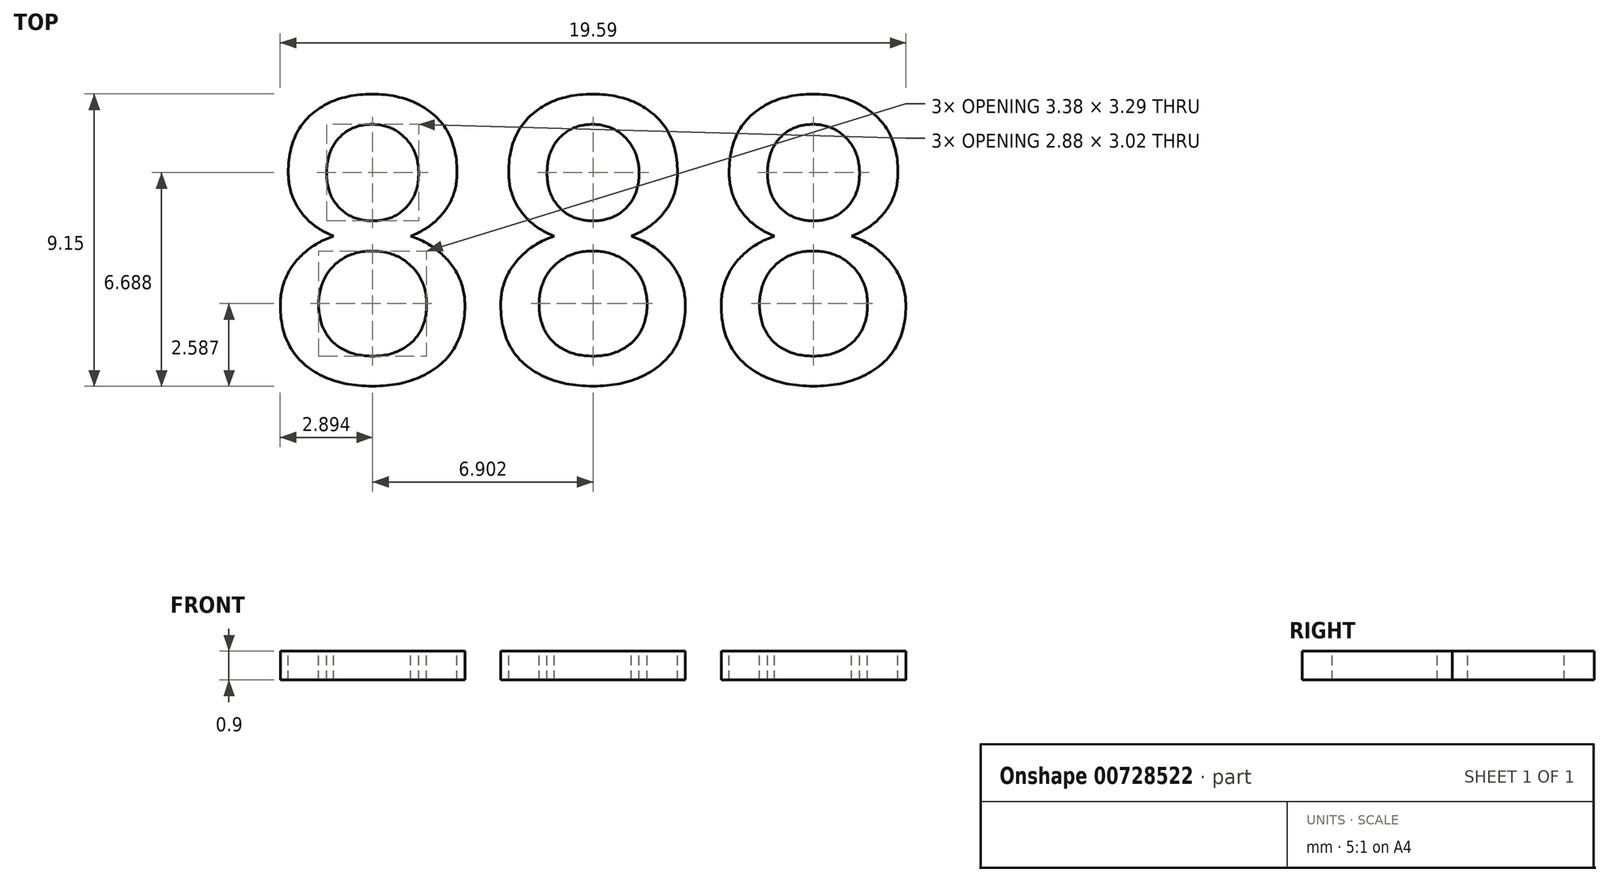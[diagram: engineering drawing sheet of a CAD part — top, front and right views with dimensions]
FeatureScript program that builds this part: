
annotation { "Feature Type Name" : "Feature", "Feature Type Description" : "" }
export const myFeature = defineFeature(function(context is Context, id is Id, definition is map)
    precondition{}
    {
        {
            var Q0;
            Q0=qCreatedBy(makeId("Top.planeOp"),FACE);
            var sketch = newSketch(context, id + "F0", { "sketchPlane" : qUnion([Q0])});
            skLineSegment(sketch, "E0.bottom", {"start": v(-23, 0) * mm, "end": v(0, 0) * mm});
            skLineSegment(sketch, "E0.top", {"start": v(-23, 14.5) * mm, "end": v(0, 14.5) * mm});
            skLineSegment(sketch, "E0.left", {"start": v(-23, 0) * mm, "end": v(-23, 14.5) * mm});
            skLineSegment(sketch, "E0.right", {"start": v(0, 0) * mm, "end": v(0, 14.5) * mm});
            skSolve(sketch);
        }
        {
            var Q0;
            Q0=makeQuery(id+"F0.imprint","IMPRINT",FACE,{"disambiguationData":[TD([[makeQuery(id+"F0.imprint","IMPRINT",EDGE,{"derivedFrom":sQuery(id+"F0.wireOp",EDGE,"E0.bottom")}),1.0]])]});
            extrude(context, id + "F1", {"entities" : qUnion([Q0]), "depth" : 1 * mm, "offsetDistance" : 25 * mm});
        }
        {
            var Q0;
            Q0=makeQuery(id+"F1.opExtrude","CAP_FACE",FACE,{"disambiguationData":[OSD([sQuery(id+"F0.wireOp",EDGE,"E0.bottom"),sQuery(id+"F0.wireOp",EDGE,"E0.top"),sQuery(id+"F0.wireOp",EDGE,"E0.left"),sQuery(id+"F0.wireOp",EDGE,"E0.right")])],"isStart":false});
            var sketch = newSketch(context, id + "F2", { "sketchPlane" : qUnion([Q0])});
            skText(sketch, "E1", { "text": "888", "fontName": "RobotoSlab-Regular.ttf"});
            skLineSegment(sketch, "E2", {"start": v(-11.5, 14.5) * mm, "end": v(-11.5, 0) * mm, "construction": true});
            skLineSegment(sketch, "E3", {"start": v(-23, 7.25) * mm, "end": v(0, 7.25) * mm, "construction": true});
            skLineSegment(sketch, "E4", {"start": v(-21.96, 7.25) * mm, "end": v(-1.04, 7.25) * mm, "construction": true});
            const initialGuessF2  = {"E1": [-0.02196, 0.00275, 1, 0, 0.009]};
            skSetInitialGuess(sketch, initialGuessF2);
            skSolve(sketch);
        }
        {
            var Q0;
            Q0=makeQuery(id+"F2.imprint","IMPRINT",FACE,{"disambiguationData":[TD([[makeQuery(id+"F2.imprint","IMPRINT",EDGE,{"derivedFrom":sQuery(id+"F2.wireOp",EDGE,"E1.sketch_text.stroke-64")}),-1.0]])]});
            var Q1;
            Q1=makeQuery(id+"F2.imprint","IMPRINT",FACE,{"disambiguationData":[TD([[makeQuery(id+"F2.imprint","IMPRINT",EDGE,{"derivedFrom":sQuery(id+"F2.wireOp",EDGE,"E1.sketch_text.stroke-32")}),-1.0]])]});
            var Q2;
            Q2=makeQuery(id+"F2.imprint","IMPRINT",FACE,{"disambiguationData":[TD([[makeQuery(id+"F2.imprint","IMPRINT",EDGE,{"derivedFrom":sQuery(id+"F2.wireOp",EDGE,"E1.sketch_text.stroke-0")}),-1.0]])]});
            extrude(context, id + "F3", {"entities" : qUnion([Q0, Q1, Q2]), "operationType" : NewBodyOperationType.INTERSECT, "oppositeDirection" : true, "depth" : 0.9 * mm, "offsetDistance" : 25 * mm});
        }
    });
